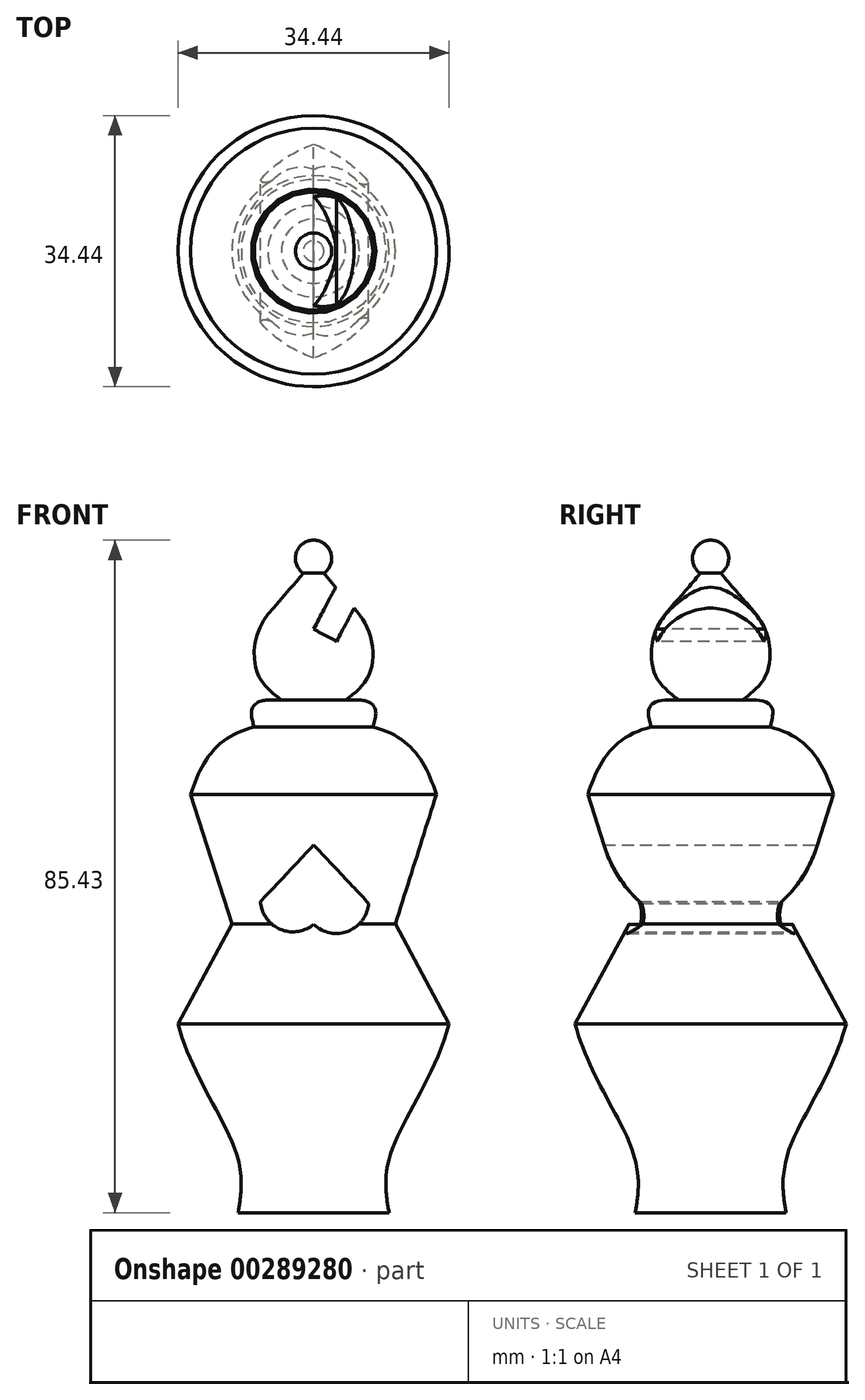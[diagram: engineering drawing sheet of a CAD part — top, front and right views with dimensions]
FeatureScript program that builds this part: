
annotation { "Feature Type Name" : "Feature", "Feature Type Description" : "" }
export const myFeature = defineFeature(function(context is Context, id is Id, definition is map)
    precondition{}
    {
        {
            var Q0;
            Q0=qCreatedBy(makeId("Front.planeOp"),FACE);
            var sketch = newSketch(context, id + "F0", { "sketchPlane" : qUnion([Q0])});
            skFitSpline(sketch, "E0", {"points": [v(2.07, 23.17) * mm, v(15.6, 13.96) * mm, v(17.22, -15.22) * mm, v(9.47, -32.86) * mm, v(10.66, -44.08) * mm], "startDerivative": vector(115.68, -2.38) * mm, "endDerivative": vector(12.2, -60.3) * mm});
            skFitSpline(sketch, "E1", {"points": [v(9.73, -39.19) * mm, v(9.22, -34.6) * mm], "startDerivative": vector(-0.3, 4.58) * mm, "endDerivative": vector(-0.3, 4.58) * mm});
            skLineSegment(sketch, "E2", {"start": v(2.07, 23.17) * mm, "end": v(0, 23.17) * mm});
            skLineSegment(sketch, "E3", {"start": v(0, 48.37) * mm, "end": v(0, -55.96) * mm});
            skLineSegment(sketch, "E4", {"start": v(11.14, 22.98) * mm, "end": v(11.14, 23.17) * mm});
            skLineSegment(sketch, "E5", {"start": v(0, 25.93) * mm, "end": v(5.81, 25.93) * mm});
            skCircle(sketch, "E6", {"center": v(0, 43.94) * mm, "radius": 2.3 * mm});
            skFitSpline(sketch, "E7", {"points": [v(1.3, 42.04) * mm, v(4.08, 38.8) * mm, v(7, 34.69) * mm, v(7.07, 29.2) * mm, v(4.07, 25.93) * mm], "startDerivative": vector(11.35, -13.57) * mm, "endDerivative": vector(-14.93, -11.59) * mm});
            skLineSegment(sketch, "E8", {"start": v(15.6, 13.96) * mm, "end": v(10.38, -2.54) * mm});
            skLineSegment(sketch, "E9", {"start": v(10.38, -2.54) * mm, "end": v(17.22, -15.22) * mm});
            skFitSpline(sketch, "E10", {"points": [v(5.81, 25.93) * mm, v(7.15, 25.62) * mm, v(7.87, 24.67) * mm, v(7.57, 22.5) * mm], "startDerivative": vector(6.03, -0.48) * mm, "endDerivative": vector(-1.38, -5.85) * mm});
            skLineSegment(sketch, "E11", {"start": v(9.73, -39.19) * mm, "end": v(0, -39.19) * mm});
            skSolve(sketch);
        }
        {
            var Q0;
            Q0=qCreatedBy(makeId("Front.planeOp"),FACE);
            var sketch = newSketch(context, id + "F1", { "sketchPlane" : qUnion([Q0])});
            skArc(sketch, "E12", {"start": v(0.02, -2.56) * mm, "mid": v(4.36, -3.44) * mm, "end": v(7, 0.12) * mm});
            skArc(sketch, "E13", {"start": v(-6.73, 0.33) * mm, "mid": v(-4.24, -3.19) * mm, "end": v(0.02, -2.56) * mm});
            skLineSegment(sketch, "E14", {"start": v(7, 0.12) * mm, "end": v(0.02, 7.51) * mm});
            skLineSegment(sketch, "E15", {"start": v(0.02, 7.51) * mm, "end": v(-6.73, 0.33) * mm});
            skSolve(sketch);
        }
        {
            var Q0;
            {var subQ0=sQuery(id+"F0.wireOp",EDGE,"cb6a9b35-9168-4a4d-8726-e04cc9f18710");Q0=makeQuery(id+"F0.imprint","IMPRINT",FACE,{"disambiguationData":[TD([[makeQuery(id+"F0.imprint","IMPRINT",EDGE,{"derivedFrom":subQ0}),-1.0]])]});}
            var Q1;
            {var subQ6=sQuery(id+"F0.wireOp",EDGE,"956ZAo7J-syZX-qupP-4Z4o-nVZysOvjX8NJ");Q1=makeQuery(id+"F0.imprint","IMPRINT",FACE,{"disambiguationData":[TD([[makeQuery(id+"F0.imprint","IMPRINT",EDGE,{"derivedFrom":subQ6}),1.0]])]});}
            var Q2;
            {var subQ0=sQuery(id+"F0.wireOp",EDGE,"E5");Q2=makeQuery(id+"F0.imprint","IMPRINT",FACE,{"disambiguationData":[TD([[makeQuery(id+"F0.imprint","IMPRINT",EDGE,{"derivedFrom":subQ0}),-1.0]])]});}
            var Q3;
            {var subQ3=sQuery(id+"F0.wireOp",EDGE,"402db0d5-4047-4234-aae8-eeb4e440a54c");Q3=makeQuery(id+"F0.imprint","IMPRINT",FACE,{"disambiguationData":[TD([[makeQuery(id+"F0.imprint","IMPRINT",EDGE,{"derivedFrom":subQ3}),-1.0]])]});}
            var Q4;
            {var subQ0=sQuery(id+"F0.wireOp",EDGE,"E6");var subQ1=sQuery(id+"F0.wireOp",EDGE,"E3");var subQ2=makeQuery(id+"F0.imprint","INTERSECT",VERTEX,{"disambiguationData":[OD(0.0)],"derivedFrom":[subQ1,subQ0]});Q4=makeQuery(id+"F0.imprint","IMPRINT",FACE,{"disambiguationData":[TD([[makeQuery(id+"F0.imprint","IMPRINT",EDGE,{"disambiguationData":[TD([[subQ2,1.0]])],"derivedFrom":subQ1}),1.0]])]});}
            var Q5;
            {var subQ5=sQuery(id+"F0.wireOp",EDGE,"E7");Q5=makeQuery(id+"F0.imprint","IMPRINT",FACE,{"disambiguationData":[TD([[makeQuery(id+"F0.imprint","IMPRINT",EDGE,{"derivedFrom":subQ5}),-1.0]])]});}
            var Q6;
            {var subQ0=sQuery(id+"F0.wireOp",EDGE,"E6");var subQ1=sQuery(id+"F0.wireOp",EDGE,"E3");var subQ2=makeQuery(id+"F0.imprint","INTERSECT",VERTEX,{"disambiguationData":[OD(0.0)],"derivedFrom":[subQ1,subQ0]});Q6=makeQuery(id+"F0.imprint","IMPRINT",FACE,{"disambiguationData":[TD([[makeQuery(id+"F0.imprint","IMPRINT",EDGE,{"disambiguationData":[TD([[subQ2,-1.0]])],"derivedFrom":subQ1}),1.0]])]});}
            var Q7;
            {var subQ1=sQuery(id+"F0.wireOp",EDGE,"E0");Q7=makeQuery(id+"F0.imprint","IMPRINT",FACE,{"disambiguationData":[TD([[makeQuery(id+"F0.imprint","IMPRINT",EDGE,{"derivedFrom":subQ1}),-1.0]])]});}
            var Q8;
            Q8=makeQuery(id+"F0.imprint","IMPRINT",FACE,{"disambiguationData":[TD([[makeQuery(id+"F0.imprint","IMPRINT",EDGE,{"derivedFrom":sQuery(id+"F0.wireOp",EDGE,"nCa9rpF8-6SNb-VAgB-uELS-ghjmVd6RV9Lh")}),1.0]])]});
            var Q9;
            Q9=sQuery(id+"F0.wireOp",EDGE,"E3");
            revolve(context, id + "F2", {"entities" : qUnion([Q0, Q1, Q2, Q3, Q4, Q5, Q6, Q7, Q8]), "axis" : qUnion([Q9]), "revolveType" : RevolveType.FULL});
        }
        {
            var Q0;
            Q0 = qSketchRegion(id + "F1", true);
            var Q1;
            Q1=sQuery(id+"F1.wireOp",EDGE,"E13");
            var Q2;
            Q2=sQuery(id+"F1.wireOp",EDGE,"E14");
            var Q3;
            Q3=sQuery(id+"F1.wireOp",EDGE,"E12");
            var Q4;
            Q4=sQuery(id+"F1.wireOp",EDGE,"E15");
            extrude(context, id + "F3", {"entities" : qUnion([Q0]), "operationType" : NewBodyOperationType.REMOVE, "surfaceEntities" : qUnion([Q1, Q2, Q3, Q4]), "endBound" : BoundingType.SYMMETRIC, "depth" : 47.75 * mm});
        }
        {
            var Q0;
            Q0=qCreatedBy(makeId("Front.planeOp"),FACE);
            var sketch = newSketch(context, id + "F4", { "sketchPlane" : qUnion([Q0])});
            skLineSegment(sketch, "E16.bottom", {"start": v(9.05, 52.11) * mm, "end": v(11.98, 50.57) * mm});
            skLineSegment(sketch, "E16.top", {"start": v(0, 34.94) * mm, "end": v(2.93, 33.4) * mm});
            skLineSegment(sketch, "E16.left", {"start": v(9.05, 52.11) * mm, "end": v(0, 34.94) * mm});
            skLineSegment(sketch, "E16.right", {"start": v(11.98, 50.57) * mm, "end": v(2.93, 33.4) * mm});
            skSolve(sketch);
        }
        {
            var Q0;
            Q0=makeQuery(id+"F4.imprint","IMPRINT",FACE,{"disambiguationData":[TD([[makeQuery(id+"F4.imprint","IMPRINT",EDGE,{"derivedFrom":sQuery(id+"F4.wireOp",EDGE,"E16.bottom")}),-1.0]])]});
            extrude(context, id + "F5", {"entities" : qUnion([Q0]), "operationType" : NewBodyOperationType.REMOVE, "endBound" : BoundingType.SYMMETRIC, "oppositeDirection" : true, "depth" : 25.4 * mm});
        }
        {
            var Q0;
            Q0=qCreatedBy(makeId("Front.planeOp"),FACE);
            var sketch = newSketch(context, id + "F6", { "sketchPlane" : qUnion([Q0])});
            skLineSegment(sketch, "E17", {"start": v(0, -52.69) * mm, "end": v(20.21, -52.69) * mm});
            skLineSegment(sketch, "E18", {"start": v(16.47, -39.19) * mm, "end": v(11.63, -39.19) * mm});
            skLineSegment(sketch, "E19", {"start": v(16.47, -44.94) * mm, "end": v(20.21, -44.94) * mm});
            skArc(sketch, "E20", {"start": v(16.47, -44.94) * mm, "mid": v(18.62, -42.06) * mm, "end": v(16.47, -39.19) * mm});
            skLineSegment(sketch, "E21", {"start": v(20.21, -52.69) * mm, "end": v(21.97, -52.69) * mm});
            skArc(sketch, "E22", {"start": v(21.97, -52.69) * mm, "mid": v(23.77, -48.2) * mm, "end": v(20.21, -44.94) * mm});
            skLineSegment(sketch, "E23", {"start": v(11.63, -39.19) * mm, "end": v(0, -39.19) * mm});
            skSolve(sketch);
        }
        {
            var Q0;
            Q0=sQuery(id+"F6.wireOp",EDGE,"E21");
            var Q1;
            Q1=sQuery(id+"F6.wireOp",EDGE,"E17");
            var Q2;
            Q2=sQuery(id+"F6.wireOp",EDGE,"E22");
            var Q3;
            Q3=sQuery(id+"F6.wireOp",EDGE,"E19");
            var Q4;
            Q4=sQuery(id+"F6.wireOp",EDGE,"E20");
            var Q5;
            Q5=sQuery(id+"F6.wireOp",EDGE,"E18");
            var Q6;
            Q6=sQuery(id+"F6.wireOp",EDGE,"E23");
            var Q7;
            Q7=sQuery(id+"F0.wireOp",EDGE,"E3");
            revolve(context, id + "F7", {"bodyType" : ToolBodyType.SURFACE, "surfaceEntities" : qUnion([Q0, Q1, Q2, Q3, Q4, Q5, Q6]), "axis" : qUnion([Q7]), "revolveType" : RevolveType.FULL});
        }
    });
